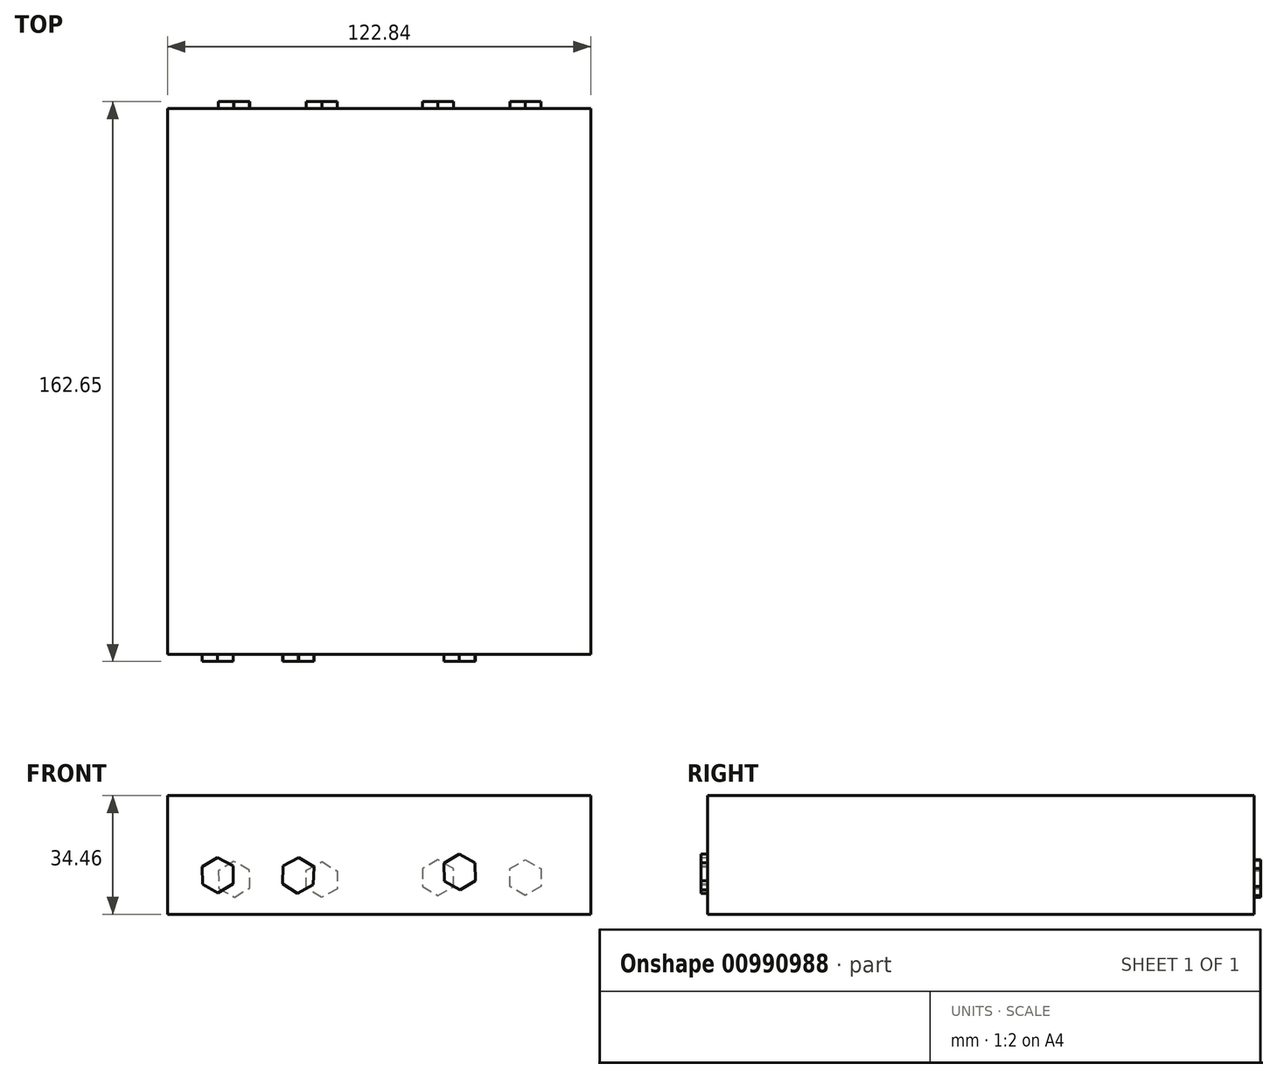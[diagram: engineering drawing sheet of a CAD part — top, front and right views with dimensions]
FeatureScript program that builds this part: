
annotation { "Feature Type Name" : "Feature", "Feature Type Description" : "" }
export const myFeature = defineFeature(function(context is Context, id is Id, definition is map)
    precondition{}
    {
        {
            var Q0;
            Q0=qCreatedBy(makeId("Front.planeOp"),FACE);
            var sketch = newSketch(context, id + "F0", { "sketchPlane" : qUnion([Q0])});
            skLineSegment(sketch, "E0.bottom", {"start": v(61.43, -17.23) * mm, "end": v(-61.42, -17.23) * mm});
            skLineSegment(sketch, "E0.top", {"start": v(61.42, 17.23) * mm, "end": v(-61.43, 17.22) * mm});
            skLineSegment(sketch, "E0.left", {"start": v(61.43, -17.23) * mm, "end": v(61.42, 17.23) * mm});
            skLineSegment(sketch, "E0.right", {"start": v(-61.42, -17.23) * mm, "end": v(-61.43, 17.22) * mm});
            skPoint(sketch, "E0.middle", {"position": v(0, 0) * mm});
            skSolve(sketch);
        }
        {
            var Q0;
            Q0=qCreatedBy(makeId("Front.planeOp"),FACE);
            var sketch = newSketch(context, id + "F1", { "sketchPlane" : qUnion([Q0])});
            skCircle(sketch, "E1.cCircle", {"center": v(-46.93, -5.9) * mm, "radius": 4.5 * mm, "construction": true});
            skLineSegment(sketch, "E1.0", {"start": v(-42.39, -8.43) * mm, "end": v(-46.84, -11.1) * mm});
            skLineSegment(sketch, "E1.1", {"start": v(-46.84, -11.1) * mm, "end": v(-51.38, -8.58) * mm});
            skLineSegment(sketch, "E1.2", {"start": v(-51.38, -8.58) * mm, "end": v(-51.47, -3.38) * mm});
            skLineSegment(sketch, "E1.3", {"start": v(-51.47, -3.38) * mm, "end": v(-47.02, -0.71) * mm});
            skLineSegment(sketch, "E1.4", {"start": v(-47.02, -0.71) * mm, "end": v(-42.47, -3.23) * mm});
            skLineSegment(sketch, "E1.5", {"start": v(-42.47, -3.23) * mm, "end": v(-42.39, -8.43) * mm});
            skPoint(sketch, "E1.0.midPoint", {"position": v(-44.61, -9.76) * mm});
            skCircle(sketch, "E2.cCircle", {"center": v(-23.56, -5.94) * mm, "radius": 4.5 * mm, "construction": true});
            skLineSegment(sketch, "E2.0", {"start": v(-19.14, -8.68) * mm, "end": v(-23.73, -11.13) * mm});
            skLineSegment(sketch, "E2.1", {"start": v(-23.73, -11.13) * mm, "end": v(-28.14, -8.39) * mm});
            skLineSegment(sketch, "E2.2", {"start": v(-28.14, -8.39) * mm, "end": v(-27.97, -3.2) * mm});
            skLineSegment(sketch, "E2.3", {"start": v(-27.97, -3.2) * mm, "end": v(-23.39, -0.74) * mm});
            skLineSegment(sketch, "E2.4", {"start": v(-23.39, -0.74) * mm, "end": v(-18.98, -3.48) * mm});
            skLineSegment(sketch, "E2.5", {"start": v(-18.98, -3.48) * mm, "end": v(-19.14, -8.68) * mm});
            skPoint(sketch, "E2.0.midPoint", {"position": v(-21.44, -9.9) * mm});
            skCircle(sketch, "E3.cCircle", {"center": v(23.36, -5) * mm, "radius": 4.5 * mm, "construction": true});
            skLineSegment(sketch, "E3.0", {"start": v(27.9, -7.52) * mm, "end": v(23.45, -10.2) * mm});
            skLineSegment(sketch, "E3.1", {"start": v(23.45, -10.2) * mm, "end": v(18.9, -7.68) * mm});
            skLineSegment(sketch, "E3.2", {"start": v(18.9, -7.68) * mm, "end": v(18.82, -2.48) * mm});
            skLineSegment(sketch, "E3.3", {"start": v(18.82, -2.48) * mm, "end": v(23.27, 0.2) * mm});
            skLineSegment(sketch, "E3.4", {"start": v(23.27, 0.2) * mm, "end": v(27.82, -2.32) * mm});
            skLineSegment(sketch, "E3.5", {"start": v(27.82, -2.32) * mm, "end": v(27.9, -7.52) * mm});
            skPoint(sketch, "E3.0.midPoint", {"position": v(25.68, -8.86) * mm});
            skSolve(sketch);
        }
        {
            var Q0;
            Q0 = qSketchRegion(id + "F0", true);
            extrude(context, id + "F2", {"entities" : qUnion([Q0]), "oppositeDirection" : true, "depth" : 158.65 * mm, "offsetDistance" : 25 * mm});
        }
        {
            var Q0;
            Q0 = qSketchRegion(id + "F1", true);
            extrude(context, id + "F3", {"entities" : qUnion([Q0]), "operationType" : NewBodyOperationType.ADD, "depth" : 2 * mm, "offsetDistance" : 25 * mm});
        }
        {
            var Q0;
            Q0=makeQuery(id+"F2.opExtrude","CAP_FACE",FACE,{"disambiguationData":[OSD([sQuery(id+"F0.wireOp",EDGE,"E0.bottom"),sQuery(id+"F0.wireOp",EDGE,"E0.top"),sQuery(id+"F0.wireOp",EDGE,"E0.left"),sQuery(id+"F0.wireOp",EDGE,"E0.right")])],"isStart":false});
            var sketch = newSketch(context, id + "F4", { "sketchPlane" : qUnion([Q0])});
            skLineSegment(sketch, "E4.bottom", {"start": v(-11.32, -16.44) * mm, "end": v(-48.54, -16.44) * mm});
            skLineSegment(sketch, "E4.top", {"start": v(-11.32, 3.23) * mm, "end": v(-48.54, 3.23) * mm});
            skLineSegment(sketch, "E4.left", {"start": v(-6.32, -11.44) * mm, "end": v(-6.32, -1.77) * mm});
            skLineSegment(sketch, "E4.right", {"start": v(-53.54, -11.44) * mm, "end": v(-53.54, -1.77) * mm});
            skPoint(sketch, "E4.middle", {"position": v(-29.93, -6.6) * mm});
            skPoint(sketch, "E5.visualSharp", {"position": v(-53.54, 3.23) * mm});
            skArc(sketch, "E5.filletArc", {"start": v(-48.54, 3.23) * mm, "mid": v(-52.08, 1.77) * mm, "end": v(-53.54, -1.77) * mm});
            skPoint(sketch, "E6.visualSharp", {"position": v(-53.54, -16.44) * mm});
            skArc(sketch, "E6.filletArc", {"start": v(-53.54, -11.44) * mm, "mid": v(-52.08, -14.98) * mm, "end": v(-48.54, -16.44) * mm});
            skPoint(sketch, "E7.visualSharp", {"position": v(-6.32, -16.44) * mm});
            skArc(sketch, "E7.filletArc", {"start": v(-11.32, -16.44) * mm, "mid": v(-7.79, -14.98) * mm, "end": v(-6.32, -11.44) * mm});
            skPoint(sketch, "E8.visualSharp", {"position": v(-6.32, 3.23) * mm});
            skArc(sketch, "E8.filletArc", {"start": v(-6.32, -1.77) * mm, "mid": v(-7.79, 1.77) * mm, "end": v(-11.32, 3.23) * mm});
            skArc(sketch, "E9.MirrorCS", {"start": v(48.54, 3.23) * mm, "mid": v(52.08, 1.77) * mm, "end": v(53.54, -1.77) * mm});
            skArc(sketch, "E10.MirrorCS", {"start": v(6.32, -1.77) * mm, "mid": v(7.79, 1.77) * mm, "end": v(11.32, 3.23) * mm});
            skArc(sketch, "E11.MirrorCS", {"start": v(53.54, -11.44) * mm, "mid": v(52.08, -14.98) * mm, "end": v(48.54, -16.44) * mm});
            skArc(sketch, "E12.MirrorCS", {"start": v(11.32, -16.44) * mm, "mid": v(7.79, -14.98) * mm, "end": v(6.32, -11.44) * mm});
            skPoint(sketch, "E13.MirrorP", {"position": v(29.93, -6.6) * mm});
            skPoint(sketch, "E14.MirrorP", {"position": v(53.54, 3.23) * mm});
            skPoint(sketch, "E15.MirrorP", {"position": v(6.32, 3.23) * mm});
            skPoint(sketch, "E16.MirrorP", {"position": v(6.32, -16.44) * mm});
            skPoint(sketch, "E17.MirrorP", {"position": v(53.54, -16.44) * mm});
            skLineSegment(sketch, "E18.MirrorCS", {"start": v(11.32, -16.44) * mm, "end": v(48.54, -16.44) * mm});
            skLineSegment(sketch, "E19.MirrorCS", {"start": v(6.32, -11.44) * mm, "end": v(6.32, -1.77) * mm});
            skLineSegment(sketch, "E20.MirrorCS", {"start": v(11.32, 3.23) * mm, "end": v(48.54, 3.23) * mm});
            skLineSegment(sketch, "E21.MirrorCS", {"start": v(53.54, -11.44) * mm, "end": v(53.54, -1.77) * mm});
            skSolve(sketch);
        }
        {
            var Q0;
            Q0=makeQuery(id+"F4.imprint","IMPRINT",FACE,{"disambiguationData":[TD([[makeQuery(id+"F4.imprint","IMPRINT",EDGE,{"derivedFrom":sQuery(id+"F4.wireOp",EDGE,"E4.bottom")}),1.0]])]});
            var sketch = newSketch(context, id + "F5", { "sketchPlane" : qUnion([Q0])});
            skLineSegment(sketch, "E22", {"start": v(29.48, -25.71) * mm, "end": v(29.48, 25.7) * mm, "construction": true});
            skLineSegment(sketch, "E23", {"start": v(-29.72, 25.88) * mm, "end": v(-29.72, -25.8) * mm, "construction": true});
            skCircle(sketch, "E24.MirrorC", {"center": v(-42.84, -7.17) * mm, "radius": 6 * mm});
            skCircle(sketch, "E25.MirrorC", {"center": v(-16.6, -7.17) * mm, "radius": 6 * mm});
            skCircle(sketch, "E26.MirrorC", {"center": v(16.6, -7.17) * mm, "radius": 6 * mm});
            skCircle(sketch, "E27.MirrorC", {"center": v(42.35, -7.17) * mm, "radius": 6 * mm});
            skSolve(sketch);
        }
        {
            var Q0;
            Q0=makeQuery(id+"F4.imprint","IMPRINT",FACE,{"disambiguationData":[TD([[makeQuery(id+"F4.imprint","IMPRINT",EDGE,{"derivedFrom":sQuery(id+"F4.wireOp",EDGE,"E4.bottom")}),1.0]])]});
            var sketch = newSketch(context, id + "F6", { "sketchPlane" : qUnion([Q0])});
            skCircle(sketch, "E28.cCircle", {"center": v(42.14, -7.1) * mm, "radius": 4.5 * mm, "construction": true});
            skLineSegment(sketch, "E28.0", {"start": v(42.03, -12.29) * mm, "end": v(37.59, -9.6) * mm});
            skLineSegment(sketch, "E28.1", {"start": v(37.59, -9.6) * mm, "end": v(37.7, -4.4) * mm});
            skLineSegment(sketch, "E28.2", {"start": v(37.7, -4.4) * mm, "end": v(42.25, -1.9) * mm});
            skLineSegment(sketch, "E28.3", {"start": v(42.25, -1.9) * mm, "end": v(46.7, -4.6) * mm});
            skLineSegment(sketch, "E28.4", {"start": v(46.7, -4.6) * mm, "end": v(46.58, -9.79) * mm});
            skLineSegment(sketch, "E28.5", {"start": v(46.58, -9.79) * mm, "end": v(42.03, -12.29) * mm});
            skPoint(sketch, "E28.0.midPoint", {"position": v(39.8, -10.94) * mm});
            skLineSegment(sketch, "E29.MirrorCS", {"start": v(21.24, -9.67) * mm, "end": v(21.24, -4.47) * mm});
            skPoint(sketch, "E30.MirrorP", {"position": v(19.02, -11.02) * mm});
            skLineSegment(sketch, "E31.MirrorCS", {"start": v(12.25, -4.67) * mm, "end": v(12.25, -9.86) * mm});
            skCircle(sketch, "E32.MirrorC", {"center": v(16.7, -7.17) * mm, "radius": 4.5 * mm, "construction": true});
            skLineSegment(sketch, "E33.MirrorCS", {"start": v(16.8, -12.36) * mm, "end": v(21.24, -9.67) * mm});
            skLineSegment(sketch, "E34.MirrorCS", {"start": v(12.25, -9.86) * mm, "end": v(16.8, -12.36) * mm});
            skLineSegment(sketch, "E35.MirrorCS", {"start": v(16.7, -1.97) * mm, "end": v(12.25, -4.67) * mm});
            skLineSegment(sketch, "E36.MirrorCS", {"start": v(21.24, -4.47) * mm, "end": v(16.7, -1.97) * mm});
            skCircle(sketch, "E37.cCircle", {"center": v(-17.02, -6.6) * mm, "radius": 4.5 * mm, "construction": true});
            skLineSegment(sketch, "E37.0", {"start": v(-17.02, -11.8) * mm, "end": v(-21.52, -9.2) * mm});
            skLineSegment(sketch, "E37.1", {"start": v(-21.52, -9.2) * mm, "end": v(-21.52, -4) * mm});
            skLineSegment(sketch, "E37.2", {"start": v(-21.52, -4) * mm, "end": v(-17.02, -1.4) * mm});
            skLineSegment(sketch, "E37.3", {"start": v(-17.02, -1.4) * mm, "end": v(-12.52, -4) * mm});
            skLineSegment(sketch, "E37.4", {"start": v(-12.52, -4) * mm, "end": v(-12.52, -9.2) * mm});
            skLineSegment(sketch, "E37.5", {"start": v(-12.52, -9.2) * mm, "end": v(-17.02, -11.8) * mm});
            skPoint(sketch, "E37.0.midPoint", {"position": v(-19.27, -10.5) * mm});
            skLineSegment(sketch, "E38.MirrorCS", {"start": v(-46.92, -4) * mm, "end": v(-46.92, -9.2) * mm});
            skLineSegment(sketch, "E39.MirrorCS", {"start": v(-37.92, -9.2) * mm, "end": v(-37.92, -4) * mm});
            skCircle(sketch, "E40.MirrorC", {"center": v(-42.42, -6.6) * mm, "radius": 4.5 * mm, "construction": true});
            skLineSegment(sketch, "E41.MirrorCS", {"start": v(-37.92, -4) * mm, "end": v(-42.42, -1.4) * mm});
            skLineSegment(sketch, "E42.MirrorCS", {"start": v(-42.42, -11.8) * mm, "end": v(-37.92, -9.2) * mm});
            skLineSegment(sketch, "E43.MirrorCS", {"start": v(-42.42, -1.4) * mm, "end": v(-46.92, -4) * mm});
            skLineSegment(sketch, "E44.MirrorCS", {"start": v(-46.92, -9.2) * mm, "end": v(-42.42, -11.8) * mm});
            skPoint(sketch, "E45.MirrorP", {"position": v(-40.17, -10.5) * mm});
            skSolve(sketch);
        }
        {
            var Q0;
            Q0 = qSketchRegion(id + "F6", true);
            extrude(context, id + "F7", {"entities" : qUnion([Q0]), "operationType" : NewBodyOperationType.ADD, "depth" : 2 * mm, "offsetDistance" : 25 * mm});
        }
    });
